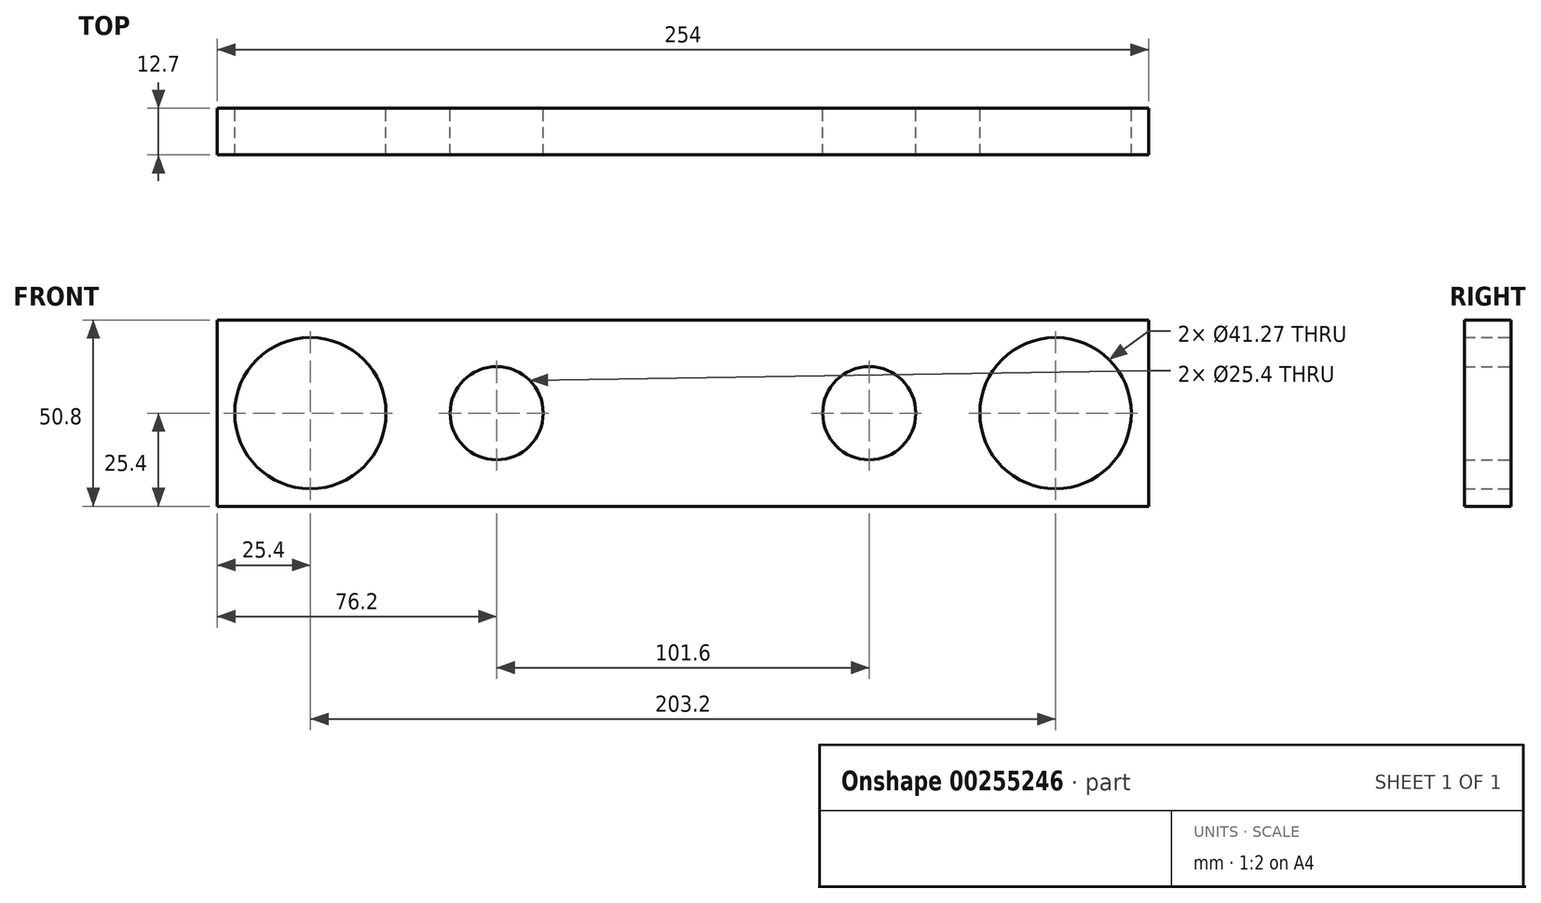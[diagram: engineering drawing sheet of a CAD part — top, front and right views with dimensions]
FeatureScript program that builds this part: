
annotation { "Feature Type Name" : "Feature", "Feature Type Description" : "" }
export const myFeature = defineFeature(function(context is Context, id is Id, definition is map)
    precondition{}
    {
        {
            var Q0;
            Q0=qCreatedBy(makeId("Front.planeOp"),FACE);
            var sketch = newSketch(context, id + "F0", { "sketchPlane" : qUnion([Q0])});
            skLineSegment(sketch, "E0.bottom", {"start": v(127, -25.4) * mm, "end": v(-127, -25.4) * mm});
            skLineSegment(sketch, "E0.top", {"start": v(127, 25.4) * mm, "end": v(-127, 25.4) * mm});
            skLineSegment(sketch, "E0.left", {"start": v(127, -25.4) * mm, "end": v(127, 25.4) * mm});
            skLineSegment(sketch, "E0.right", {"start": v(-127, -25.4) * mm, "end": v(-127, 25.4) * mm});
            skPoint(sketch, "E0.middle", {"position": v(0, 0) * mm});
            skLineSegment(sketch, "E1", {"start": v(0, 25.4) * mm, "end": v(0, -25.4) * mm, "construction": true});
            skCircle(sketch, "E2", {"center": v(-101.6, 0) * mm, "radius": 20.64 * mm});
            skPoint(sketch, "E2.centerSnap0", {"position": v(-127, 0) * mm});
            skCircle(sketch, "E3.MirrorC", {"center": v(101.6, 0) * mm, "radius": 20.64 * mm});
            skCircle(sketch, "E4", {"center": v(-50.8, 0) * mm, "radius": 12.7 * mm});
            skCircle(sketch, "E5.MirrorC", {"center": v(50.8, 0) * mm, "radius": 12.7 * mm});
            skSolve(sketch);
        }
        {
            var Q0;
            Q0=makeQuery(id+"F0.imprint","IMPRINT",FACE,{"disambiguationData":[TD([[makeQuery(id+"F0.imprint","IMPRINT",EDGE,{"derivedFrom":sQuery(id+"F0.wireOp",EDGE,"E0.bottom")}),-1.0]])]});
            extrude(context, id + "F1", {"entities" : qUnion([Q0]), "depth" : 12.7 * mm});
        }
    });
